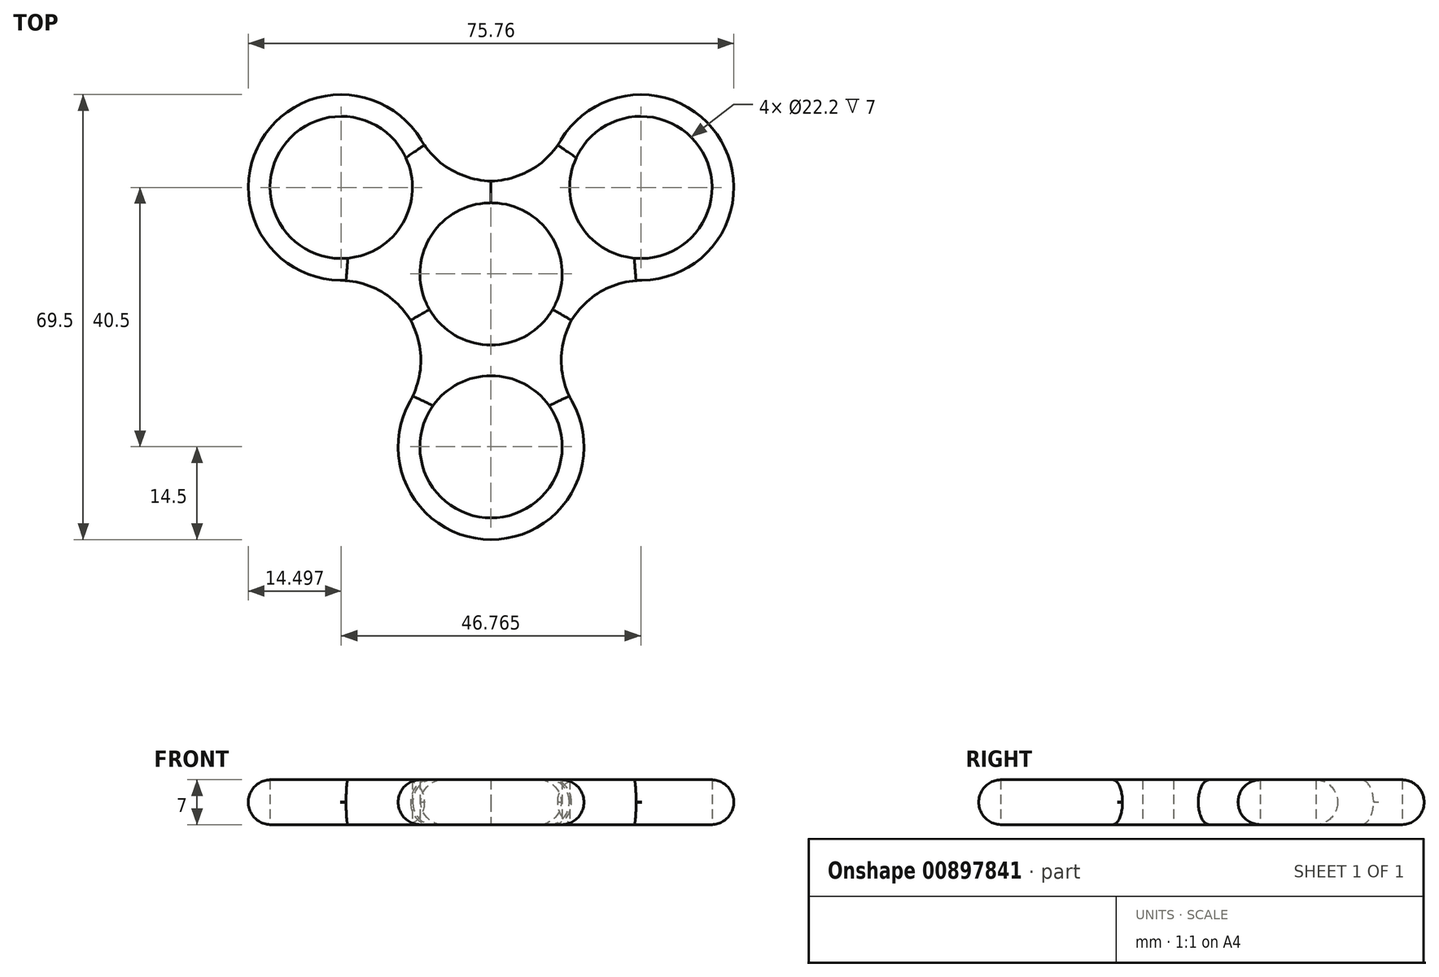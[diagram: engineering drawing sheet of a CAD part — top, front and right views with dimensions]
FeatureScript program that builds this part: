
annotation { "Feature Type Name" : "Feature", "Feature Type Description" : "" }
export const myFeature = defineFeature(function(context is Context, id is Id, definition is map)
    precondition{}
    {
        {
            var Q0;
            Q0=qCreatedBy(makeId("Top.planeOp"),FACE);
            var sketch = newSketch(context, id + "F0", { "sketchPlane" : qUnion([Q0])});
            skCircle(sketch, "E0", {"center": v(0, 0) * mm, "radius": 14.5 * mm});
            skCircle(sketch, "E1", {"center": v(0, 0) * mm, "radius": 11.1 * mm});
            skCircle(sketch, "E2", {"center": v(0, -27) * mm, "radius": 11.1 * mm});
            skCircle(sketch, "E3", {"center": v(0, -27) * mm, "radius": 14.5 * mm});
            skCircle(sketch, "E4.1.0", {"center": v(23.38, 13.5) * mm, "radius": 14.5 * mm});
            skCircle(sketch, "E4.1.1", {"center": v(23.38, 13.5) * mm, "radius": 11.1 * mm});
            skCircle(sketch, "E4.2.0", {"center": v(-23.38, 13.5) * mm, "radius": 14.5 * mm});
            skCircle(sketch, "E4.2.1", {"center": v(-23.38, 13.5) * mm, "radius": 11.1 * mm});
            skSolve(sketch);
        }
        {
            var Q0;
            Q0=makeQuery(id+"F0.imprint","IMPRINT",FACE,{"disambiguationData":[TD([[makeQuery(id+"F0.imprint","IMPRINT",EDGE,{"derivedFrom":sQuery(id+"F0.wireOp",EDGE,"E2")}),-1.0]])]});
            var Q1;
            {var subQ0=sQuery(id+"F0.wireOp",EDGE,"E3");var subQ1=sQuery(id+"F0.wireOp",EDGE,"E0");var subQ2=makeQuery(id+"F0.imprint","INTERSECT",VERTEX,{"disambiguationData":[OD(0.0)],"derivedFrom":[subQ1,subQ0]});Q1=makeQuery(id+"F0.imprint","IMPRINT",FACE,{"disambiguationData":[TD([[makeQuery(id+"F0.imprint","IMPRINT",EDGE,{"disambiguationData":[TD([[subQ2,-1.0]])],"derivedFrom":subQ1}),1.0]])]});}
            var Q2;
            Q2=makeQuery(id+"F0.imprint","IMPRINT",FACE,{"disambiguationData":[TD([[makeQuery(id+"F0.imprint","IMPRINT",EDGE,{"derivedFrom":sQuery(id+"F0.wireOp",EDGE,"E1")}),-1.0]])]});
            var Q3;
            Q3=makeQuery(id+"F0.imprint","IMPRINT",FACE,{"disambiguationData":[TD([[makeQuery(id+"F0.imprint","IMPRINT",EDGE,{"derivedFrom":sQuery(id+"F0.wireOp",EDGE,"E4.2.1")}),-1.0]])]});
            var Q4;
            {var subQ0=sQuery(id+"F0.wireOp",EDGE,"E4.2.0");var subQ1=sQuery(id+"F0.wireOp",EDGE,"E0");var subQ2=makeQuery(id+"F0.imprint","INTERSECT",VERTEX,{"disambiguationData":[OD(0.0)],"derivedFrom":[subQ1,subQ0]});Q4=makeQuery(id+"F0.imprint","IMPRINT",FACE,{"disambiguationData":[TD([[makeQuery(id+"F0.imprint","IMPRINT",EDGE,{"disambiguationData":[TD([[subQ2,-1.0]])],"derivedFrom":subQ1}),1.0]])]});}
            var Q5;
            {var subQ0=sQuery(id+"F0.wireOp",EDGE,"E4.1.0");var subQ1=sQuery(id+"F0.wireOp",EDGE,"E0");var subQ2=makeQuery(id+"F0.imprint","INTERSECT",VERTEX,{"disambiguationData":[OD(0.0)],"derivedFrom":[subQ1,subQ0]});Q5=makeQuery(id+"F0.imprint","IMPRINT",FACE,{"disambiguationData":[TD([[makeQuery(id+"F0.imprint","IMPRINT",EDGE,{"disambiguationData":[TD([[subQ2,1.0]])],"derivedFrom":subQ1}),1.0]])]});}
            var Q6;
            Q6=makeQuery(id+"F0.imprint","IMPRINT",FACE,{"disambiguationData":[TD([[makeQuery(id+"F0.imprint","IMPRINT",EDGE,{"derivedFrom":sQuery(id+"F0.wireOp",EDGE,"E4.1.1")}),-1.0]])]});
            extrude(context, id + "F1", {"entities" : qUnion([Q0, Q1, Q2, Q3, Q4, Q5, Q6]), "depth" : 7 * mm, "offsetDistance" : 25 * mm});
        }
        {
            var Q0;
            {var subQ0=sQuery(id+"F0.wireOp",EDGE,"E4.1.0");var subQ1=sQuery(id+"F0.wireOp",EDGE,"E0");Q0=makeQuery(id+"F1.opExtrude","SWEPT_EDGE",EDGE,{"disambiguationData":[OSD([subQ1,subQ0]),TDD([makeQuery(id+"F0.imprint","INTERSECT",VERTEX,{"disambiguationData":[OD(0.0)],"derivedFrom":[subQ1,subQ0]})])]});}
            var Q1;
            {var subQ0=sQuery(id+"F0.wireOp",EDGE,"E4.2.0");var subQ1=sQuery(id+"F0.wireOp",EDGE,"E0");Q1=makeQuery(id+"F1.opExtrude","SWEPT_EDGE",EDGE,{"disambiguationData":[OSD([subQ1,subQ0]),TDD([makeQuery(id+"F0.imprint","INTERSECT",VERTEX,{"disambiguationData":[OD(0.0)],"derivedFrom":[subQ1,subQ0]})])]});}
            var Q2;
            {var subQ0=sQuery(id+"F0.wireOp",EDGE,"E4.2.0");var subQ1=sQuery(id+"F0.wireOp",EDGE,"E0");Q2=makeQuery(id+"F1.opExtrude","SWEPT_EDGE",EDGE,{"disambiguationData":[OSD([subQ1,subQ0]),TDD([makeQuery(id+"F0.imprint","INTERSECT",VERTEX,{"disambiguationData":[OD(1.0)],"derivedFrom":[subQ1,subQ0]})])]});}
            var Q3;
            {var subQ0=sQuery(id+"F0.wireOp",EDGE,"E3");var subQ1=sQuery(id+"F0.wireOp",EDGE,"E0");Q3=makeQuery(id+"F1.opExtrude","SWEPT_EDGE",EDGE,{"disambiguationData":[OSD([subQ1,subQ0]),TDD([makeQuery(id+"F0.imprint","INTERSECT",VERTEX,{"disambiguationData":[OD(0.0)],"derivedFrom":[subQ1,subQ0]})])]});}
            var Q4;
            {var subQ0=sQuery(id+"F0.wireOp",EDGE,"E3");var subQ1=sQuery(id+"F0.wireOp",EDGE,"E0");Q4=makeQuery(id+"F1.opExtrude","SWEPT_EDGE",EDGE,{"disambiguationData":[OSD([subQ1,subQ0]),TDD([makeQuery(id+"F0.imprint","INTERSECT",VERTEX,{"disambiguationData":[OD(1.0)],"derivedFrom":[subQ1,subQ0]})])]});}
            var Q5;
            {var subQ0=sQuery(id+"F0.wireOp",EDGE,"E4.1.0");var subQ1=sQuery(id+"F0.wireOp",EDGE,"E0");Q5=makeQuery(id+"F1.opExtrude","SWEPT_EDGE",EDGE,{"disambiguationData":[OSD([subQ1,subQ0]),TDD([makeQuery(id+"F0.imprint","INTERSECT",VERTEX,{"disambiguationData":[OD(1.0)],"derivedFrom":[subQ1,subQ0]})])]});}
            fillet(context, id + "F2", {"entities" : qUnion([Q0, Q1, Q2, Q3, Q4, Q5]), "tangentPropagation" : true, "radius" : 13 * mm, "defaultsChanged" : false, "vertexSettings" : [], "allowEdgeOverflow" : false});
        }
        {
            var Q0;
            Q0=makeQuery(id+"F1.opExtrude","CAP_EDGE",EDGE,{"disambiguationData":[OSD([sQuery(id+"F0.wireOp",EDGE,"E4.1.0")])],"isStart":true});
            var Q1;
            Q1=makeQuery(id+"F1.opExtrude","CAP_EDGE",EDGE,{"disambiguationData":[OSD([sQuery(id+"F0.wireOp",EDGE,"E4.1.0")])],"isStart":false});
            var Q2;
            Q2=makeQuery(id+"F1.opExtrude","CAP_EDGE",EDGE,{"disambiguationData":[OSD([sQuery(id+"F0.wireOp",EDGE,"E4.2.0")])],"isStart":true});
            var Q3;
            Q3=makeQuery(id+"F1.opExtrude","CAP_EDGE",EDGE,{"disambiguationData":[OSD([sQuery(id+"F0.wireOp",EDGE,"E4.2.0")])],"isStart":false});
            var Q4;
            Q4=makeQuery(id+"F1.opExtrude","CAP_EDGE",EDGE,{"disambiguationData":[OSD([sQuery(id+"F0.wireOp",EDGE,"E3")])],"isStart":true});
            var Q5;
            Q5=makeQuery(id+"F1.opExtrude","CAP_EDGE",EDGE,{"disambiguationData":[OSD([sQuery(id+"F0.wireOp",EDGE,"E3")])],"isStart":false});
            fillet(context, id + "F3", {"entities" : qUnion([Q0, Q1, Q2, Q3, Q4, Q5]), "tangentPropagation" : true, "radius" : 3.5 * mm, "defaultsChanged" : false, "vertexSettings" : [], "allowEdgeOverflow" : false});
        }
    });
